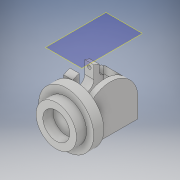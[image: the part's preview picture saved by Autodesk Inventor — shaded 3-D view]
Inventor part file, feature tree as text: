
AUTODESK INVENTOR PART (.ipt)
format: ipt  version: 2018 (Build 220112000, 112)  size: 237,056 bytes
history: native  units: in
note: dims shown in document units (in); Inventor stores cm internally (conversion verified against a paired STEP export)
features: sketch x11, extrude x10, plane x1
ambient origin geometry x8: Origin, YZ Plane, XZ Plane, XY Plane, X Axis, Y Axis, Z Axis, Center Point
bodies: Solid1 (feature_tree)
feature tree (22):
  sketch  "Sketch1"  dims[d2=0.5906in d3=1.1811in]
  extrude  "Extrusion1"  Depth=1.1811in
  extrude  "Extrusion3"  Depth=0.1969in
  extrude  "Extrusion4"  Depth=0.2953in
  extrude  "Extrusion5"  Depth=0.748in
  extrude  "Extrusion6"  Depth=0.315in
  extrude  "Extrusion7"  Depth=0.0787in
  extrude  "Extrusion8"  Depth=0.0394in
  plane  "Work Plane1"
  extrude  "Extrusion13"  Depth=0.1181in TaperAngle=0.0deg
  sketch  "Sketch13"  dims[d34=0.1969in d35=0.0in d36=-1.5748in]
  extrude  "Extrusion16"  Depth=0.5906in
  extrude  "Extrusion17"  [1 undecoded]
  sketch  "Sketch2"  dims[d4=0.1969in d5=0.0in d12=0.1969in]
  sketch  "Sketch5"  dims[d13=0.5906in d14=0.0in d15=0.2953in]
  sketch  "Sketch6"  dims[d16=0.374in d17=0.748in]
  sketch  "Sketch7"  dims[d18=0.3937in d19=0.0in d20=0.315in]
  sketch  "Sketch8"  dims[d21=0.1181in d22=0.0787in]
  sketch  "Sketch9"  dims[d23=0.1969in d24=0.0in d27=0.0394in]
  sketch  "Sketch10"  dims[d28=0.1181in d29=0.0in d30=0.1181in d31=0.0in]
  sketch  "Sketch11"  dims[d32=0.5906in d33=0.5906in]
  sketch  "Sketch16"  dims[d40=0.0787in d52=0.2362in d53=0.0in d54=0.0in d63=0.8661in d64=0.5748in d73=0.2165in d74=0.0in d75=0.2165in d76=0.0in]
note: 1 required parameter value undecoded (feature->parameter linkage not recoverable at this tier; creation-order binding heuristic only, values carry confidence <= 0.55)
